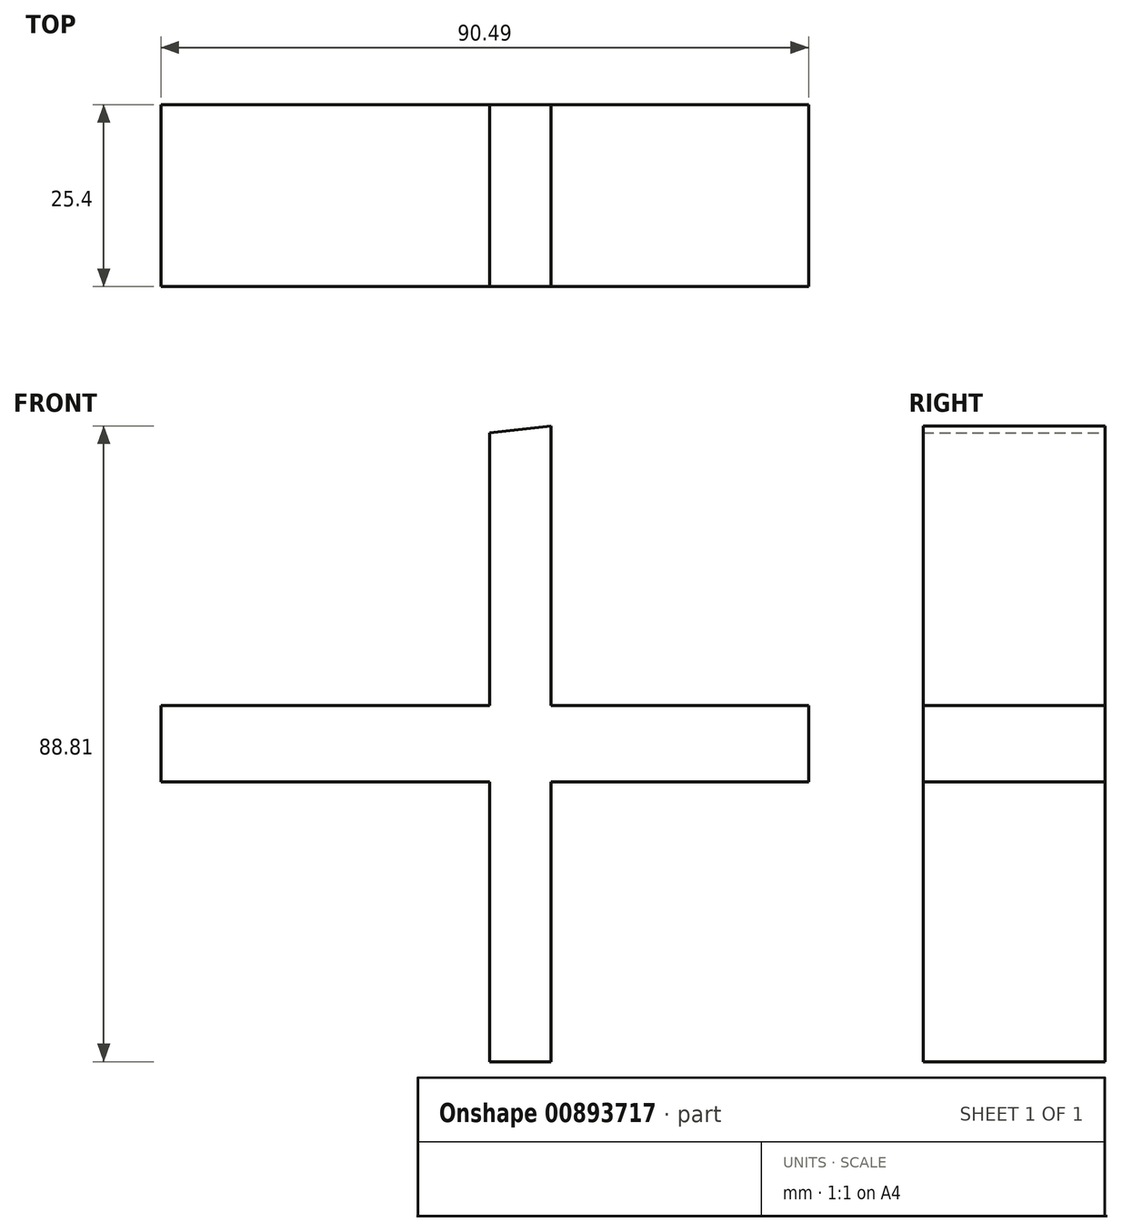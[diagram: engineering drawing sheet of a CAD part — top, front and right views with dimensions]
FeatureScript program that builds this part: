
annotation { "Feature Type Name" : "Feature", "Feature Type Description" : "" }
export const myFeature = defineFeature(function(context is Context, id is Id, definition is map)
    precondition{}
    {
        {
            var Q0;
            Q0=qCreatedBy(makeId("Front.planeOp"),FACE);
            var sketch = newSketch(context, id + "F0", { "sketchPlane" : qUnion([Q0])});
            skLineSegment(sketch, "E0.bottom", {"start": v(-54.48, 39.08) * mm, "end": v(36.01, 39.08) * mm});
            skLineSegment(sketch, "E0.top", {"start": v(-54.48, 49.76) * mm, "end": v(36.01, 49.76) * mm});
            skLineSegment(sketch, "E0.left", {"start": v(-54.48, 39.08) * mm, "end": v(-54.48, 49.76) * mm});
            skLineSegment(sketch, "E0.right", {"start": v(36.01, 39.08) * mm, "end": v(36.01, 49.76) * mm});
            skLineSegment(sketch, "E1", {"start": v(0, 88.81) * mm, "end": v(0, 0) * mm});
            skLineSegment(sketch, "E2", {"start": v(-8.57, 87.89) * mm, "end": v(-8.57, 0) * mm});
            skLineSegment(sketch, "E3", {"start": v(-8.57, 87.89) * mm, "end": v(0, 88.81) * mm});
            skLineSegment(sketch, "E4", {"start": v(0, 0) * mm, "end": v(-8.57, 0) * mm});
            skSolve(sketch);
        }
        {
            var Q0;
            Q0=makeQuery(id+"F0.imprint","IMPRINT",FACE,{"disambiguationData":[TD([[makeQuery(id+"F0.imprint","IMPRINT",EDGE,{"derivedFrom":sQuery(id+"F0.wireOp",EDGE,"5aac512f-5244-4281-9b64-7011fb725c90.bottom")}),-1.0]])]});
            var Q1;
            Q1=makeQuery(id+"F0.imprint","IMPRINT",FACE,{"disambiguationData":[TD([[makeQuery(id+"F0.imprint","IMPRINT",EDGE,{"derivedFrom":sQuery(id+"F0.wireOp",EDGE,"E0.bottom")}),1.0]])]});
            extrude(context, id + "F1", {"entities" : qUnion([Q0, Q1]), "depth" : 25.4 * mm, "offsetDistance" : 25.4 * mm});
        }
        {
            var Q0;
            {var subQ5=sQuery(id+"F0.wireOp",EDGE,"E4");Q0=makeQuery(id+"F0.imprint","IMPRINT",FACE,{"disambiguationData":[TD([[makeQuery(id+"F0.imprint","IMPRINT",EDGE,{"derivedFrom":subQ5}),-1.0]])]});}
            var Q1;
            {var subQ0=sQuery(id+"F0.wireOp",EDGE,"E2");var subQ1=sQuery(id+"F0.wireOp",EDGE,"E0.bottom");var subQ2=makeQuery(id+"F0.imprint","INTERSECT",VERTEX,{"derivedFrom":[subQ1,subQ0]});Q1=makeQuery(id+"F0.imprint","IMPRINT",FACE,{"disambiguationData":[TD([[makeQuery(id+"F0.imprint","IMPRINT",EDGE,{"disambiguationData":[TD([[subQ2,-1.0]])],"derivedFrom":subQ1}),1.0]])]});}
            var Q2;
            {var subQ5=sQuery(id+"F0.wireOp",EDGE,"E3");Q2=makeQuery(id+"F0.imprint","IMPRINT",FACE,{"disambiguationData":[TD([[makeQuery(id+"F0.imprint","IMPRINT",EDGE,{"derivedFrom":subQ5}),-1.0]])]});}
            extrude(context, id + "F2", {"entities" : qUnion([Q0, Q1, Q2]), "operationType" : NewBodyOperationType.ADD, "depth" : 25.4 * mm, "offsetDistance" : 25.4 * mm});
        }
    });
